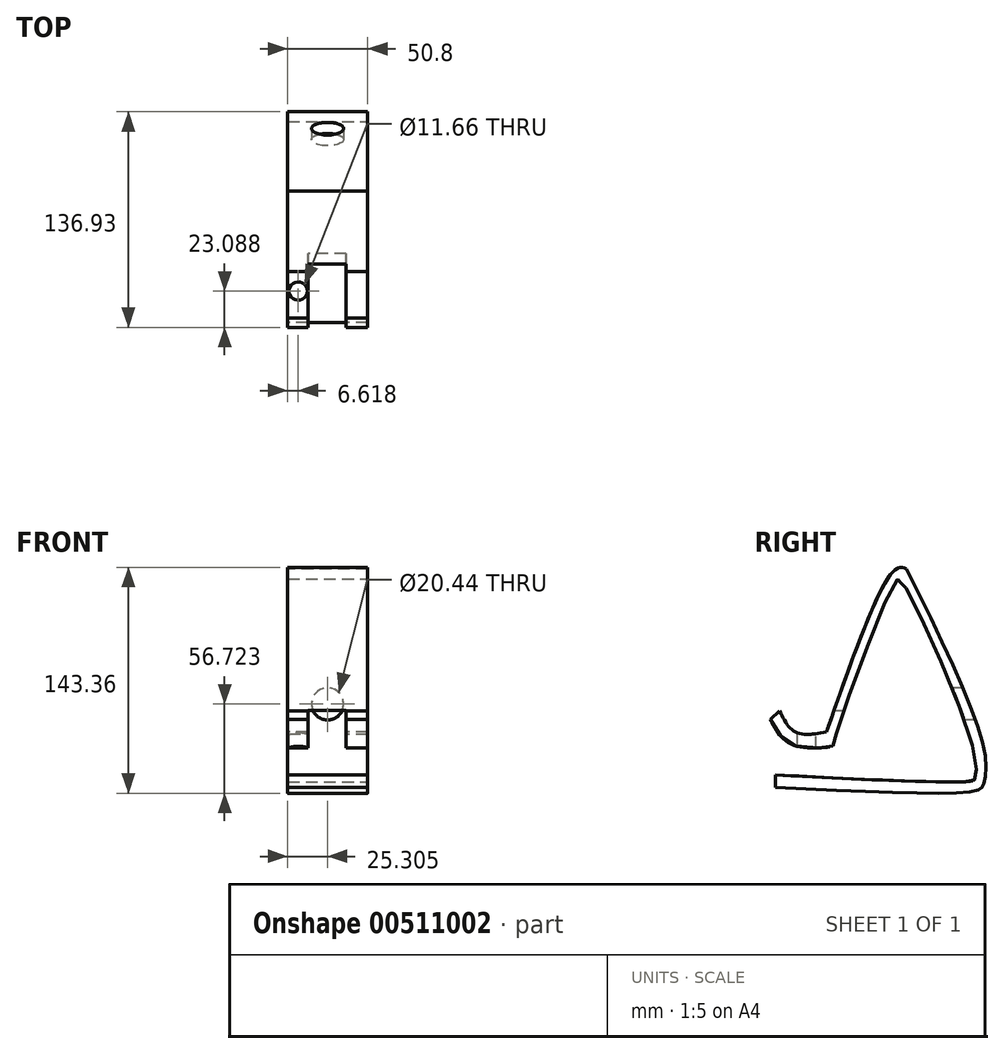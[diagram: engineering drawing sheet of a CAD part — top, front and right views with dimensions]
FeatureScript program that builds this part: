
annotation { "Feature Type Name" : "Feature", "Feature Type Description" : "" }
export const myFeature = defineFeature(function(context is Context, id is Id, definition is map)
    precondition{}
    {
        {
            var Q0;
            Q0=qCreatedBy(makeId("Right.planeOp"),FACE);
            var sketch = newSketch(context, id + "F0", { "sketchPlane" : qUnion([Q0])});
            skFitSpline(sketch, "E0", {"points": [v(0, 103.6) * mm, v(-6.72, 103.6) * mm, v(-50.96, 0) * mm], "startDerivative": vector(-32.2, 12.65) * mm, "endDerivative": vector(-63.4, -180.7) * mm});
            skFitSpline(sketch, "E1", {"points": [v(-50.96, 0) * mm, v(-70.56, 0) * mm, v(-80.64, 13.44) * mm], "startDerivative": vector(-42.1, -7.26) * mm, "endDerivative": vector(-16.93, 34.68) * mm});
            skFitSpline(sketch, "E2", {"points": [v(-83.44, -35.28) * mm, v(45.36, -36.96) * mm, v(48.72, -33.6) * mm, v(49.84, -14.56) * mm, v(0, 103.6) * mm], "startDerivative": vector(452.13, -21.04) * mm, "endDerivative": vector(-178.28, 362.06) * mm});
            skLineSegment(sketch, "E3", {"start": v(-83.44, -35.28) * mm, "end": v(-83.44, -27.13) * mm});
            skFitSpline(sketch, "E4", {"points": [v(-83.44, -27.13) * mm, v(-24.65, -30.12) * mm, v(39.63, -31.47) * mm, v(43.43, -29.84) * mm, v(40.99, -5.7) * mm, v(-2.94, 95.51) * mm, v(-6.8, 95.83) * mm, v(-45.83, -5.77) * mm, v(-47.45, -9) * mm, v(-71.64, -8.35) * mm, v(-86.47, 7.88) * mm], "startDerivative": vector(394.41, -22.03) * mm, "endDerivative": vector(-128.78, 244.6) * mm});
            skLineSegment(sketch, "E5", {"start": v(-80.64, 13.44) * mm, "end": v(-86.47, 7.88) * mm});
            skSolve(sketch);
        }
        {
            var Q0;
            Q0=makeQuery(id+"F0.imprint","IMPRINT",FACE,{"disambiguationData":[TD([[makeQuery(id+"F0.imprint","IMPRINT",EDGE,{"derivedFrom":sQuery(id+"F0.wireOp",EDGE,"E0")}),1.0]])]});
            extrude(context, id + "F1", {"entities" : qUnion([Q0]), "depth" : 50.8 * mm, "offsetDistance" : 25.4 * mm});
        }
        {
            var Q0;
            Q0=qCreatedBy(makeId("Front.planeOp"),FACE);
            var sketch = newSketch(context, id + "F2", { "sketchPlane" : qUnion([Q0])});
            skCircle(sketch, "E6", {"center": v(25.3, 17.91) * mm, "radius": 10.22 * mm});
            skSolve(sketch);
        }
        {
            var Q0;
            Q0 = qSketchRegion(id + "F2", true);
            extrude(context, id + "F3", {"entities" : qUnion([Q0]), "operationType" : NewBodyOperationType.REMOVE, "oppositeDirection" : true, "depth" : 50.8 * mm, "offsetDistance" : 25.4 * mm});
        }
        {
            var Q0;
            Q0=qCreatedBy(makeId("Front.planeOp"),FACE);
            var sketch = newSketch(context, id + "F4", { "sketchPlane" : qUnion([Q0])});
            skLineSegment(sketch, "E7.bottom", {"start": v(12.94, 13.6) * mm, "end": v(37.1, 13.6) * mm});
            skLineSegment(sketch, "E7.top", {"start": v(12.94, -10.55) * mm, "end": v(37.1, -10.55) * mm});
            skLineSegment(sketch, "E7.left", {"start": v(12.94, 13.6) * mm, "end": v(12.94, -10.55) * mm});
            skLineSegment(sketch, "E7.right", {"start": v(37.1, 13.6) * mm, "end": v(37.1, -10.55) * mm});
            skSolve(sketch);
        }
        {
            var Q0;
            Q0 = qSketchRegion(id + "F4", true);
            extrude(context, id + "F5", {"entities" : qUnion([Q0]), "operationType" : NewBodyOperationType.REMOVE, "depth" : 127 * mm, "offsetDistance" : 25.4 * mm});
        }
        {
            var Q0;
            Q0=qCreatedBy(makeId("Top.planeOp"),FACE);
            var sketch = newSketch(context, id + "F6", { "sketchPlane" : qUnion([Q0])});
            skCircle(sketch, "E8", {"center": v(6.62, -63.38) * mm, "radius": 5.83 * mm});
            skSolve(sketch);
        }
        {
            var Q0;
            Q0 = qSketchRegion(id + "F6", true);
            extrude(context, id + "F7", {"entities" : qUnion([Q0]), "operationType" : NewBodyOperationType.REMOVE, "oppositeDirection" : true, "depth" : 12.7 * mm, "offsetDistance" : 25.4 * mm});
        }
    });
